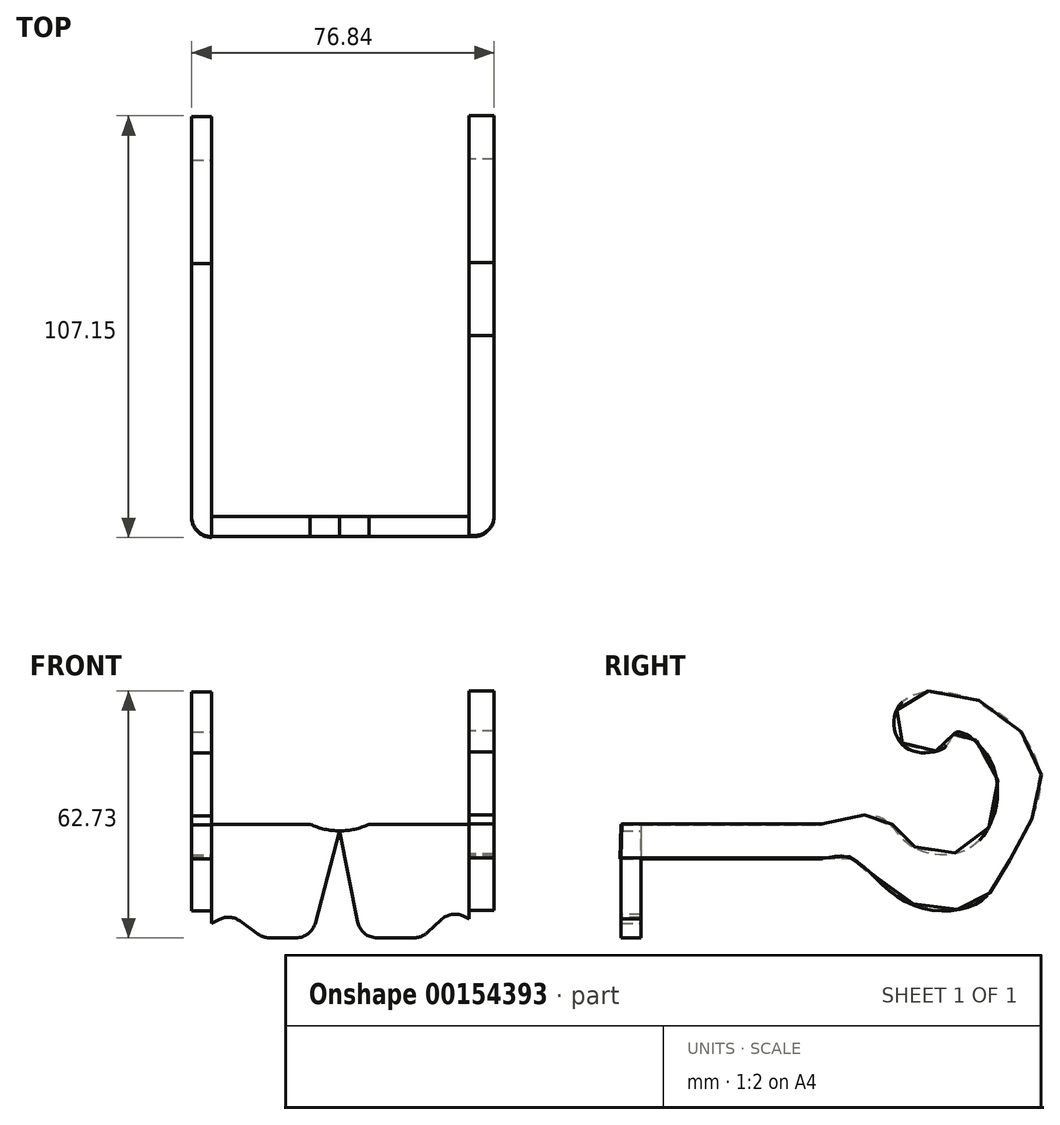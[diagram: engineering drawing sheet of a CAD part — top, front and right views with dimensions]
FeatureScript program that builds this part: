
annotation { "Feature Type Name" : "Feature", "Feature Type Description" : "" }
export const myFeature = defineFeature(function(context is Context, id is Id, definition is map)
    precondition{}
    {
        {
            var Q0;
            Q0=qCreatedBy(makeId("Right.planeOp"),FACE);
            var sketch = newSketch(context, id + "F0", { "sketchPlane" : qUnion([Q0])});
            skLineSegment(sketch, "E0", {"start": v(-32.1, 8.66) * mm, "end": v(18.7, 8.66) * mm});
            skLineSegment(sketch, "E1", {"start": v(-32.33, 0) * mm, "end": v(18.7, 0) * mm});
            skFitSpline(sketch, "E2", {"points": [v(18.7, 0) * mm, v(26.79, 0) * mm, v(39.95, -10.74) * mm, v(58.19, -11.43) * mm, v(66.73, 0) * mm, v(74.58, 20.44) * mm, v(59.57, 39.6) * mm, v(39.02, 39.6) * mm, v(39.72, 28.75) * mm, v(50.34, 28.52) * mm, v(53.1, 32.21) * mm, v(62.58, 23.2) * mm, v(57.03, 3.12) * mm, v(41.1, 3.58) * mm, v(34.4, 10.28) * mm, v(18.7, 8.66) * mm], "startDerivative": vector(163.45, 38.4) * mm, "endDerivative": vector(-264.4, -70.5) * mm});
            skLineSegment(sketch, "E3", {"start": v(-32.1, 8.66) * mm, "end": v(-32.33, 0) * mm});
            skSolve(sketch);
        }
        {
            var Q0;
            Q0=makeQuery(id+"F0.imprint","IMPRINT",FACE,{"disambiguationData":[TD([[makeQuery(id+"F0.imprint","IMPRINT",EDGE,{"derivedFrom":sQuery(id+"F0.wireOp",EDGE,"E0")}),-1.0]])]});
            extrude(context, id + "F1", {"entities" : qUnion([Q0]), "depth" : 5.08 * mm});
        }
        {
            var Q0;
            Q0=makeQuery(id+"F1.opExtrude","SWEPT_EDGE",EDGE,{"disambiguationData":[OSD([sQuery(id+"F0.wireOp",EDGE,"E0"),sQuery(id+"F0.wireOp",EDGE,"E2")])]});
            var Q1;
            Q1=makeQuery(id+"F1.opExtrude","SWEPT_EDGE",EDGE,{"disambiguationData":[OSD([sQuery(id+"F0.wireOp",EDGE,"E1"),sQuery(id+"F0.wireOp",EDGE,"E2")])]});
            fillet(context, id + "F2", {"entities" : qUnion([Q0, Q1]), "radius" : 5.08 * mm, "tangentPropagation" : true, "allowEdgeOverflow" : false});
        }
        {
            var Q0;
            Q0=makeQuery(id+"F1.opExtrude","SWEPT_BODY",BODY,{"disambiguationData":[OSD([sQuery(id+"F0.wireOp",EDGE,"E0"),sQuery(id+"F0.wireOp",EDGE,"E1"),sQuery(id+"F0.wireOp",EDGE,"E2"),sQuery(id+"F0.wireOp",EDGE,"E3")])]});
            var Q1;
            Q1=qCreatedBy(makeId("Origin.pointOp"),VERTEX);
            transform(context, id + "F3", {"entities" : qUnion([Q0]), "transformType" : TransformType.TRANSLATION_3D, "dx" : -67.94 * mm, "dy" : 0 * mm, "dz" : 0 * mm, "makeCopy" : false});
        }
        {
            var Q0;
            Q0=qCreatedBy(makeId("Front.planeOp"),FACE);
            var sketch = newSketch(context, id + "F4", { "sketchPlane" : qUnion([Q0])});
            skLineSegment(sketch, "E4", {"start": v(-40.09, 0) * mm, "end": v(-14.96, 0) * mm});
            skLineSegment(sketch, "E5", {"start": v(25.4, 0) * mm, "end": v(0, 0) * mm});
            skArc(sketch, "E6", {"start": v(-14.96, 0) * mm, "mid": v(-7.48, -1.67) * mm, "end": v(0, 0) * mm});
            skLineSegment(sketch, "E7", {"start": v(-14.64, -28.85) * mm, "end": v(-26.94, -28.85) * mm});
            skLineSegment(sketch, "E8", {"start": v(2705.78, 106.26) * mm, "end": v(2705.78, 111.84) * mm});
            skLineSegment(sketch, "E9", {"start": v(-40.09, 0) * mm, "end": v(-40.09, -25.17) * mm});
            skLineSegment(sketch, "E10", {"start": v(-40.09, -25.17) * mm, "end": v(-35.24, -22.81) * mm});
            skLineSegment(sketch, "E11", {"start": v(-35.24, -22.81) * mm, "end": v(-26.94, -28.85) * mm});
            skLineSegment(sketch, "E12", {"start": v(25.4, 0) * mm, "end": v(25.4, -24) * mm});
            skPoint(sketch, "E12.endSnap0", {"position": v(-37.66, -24) * mm});
            skLineSegment(sketch, "E13", {"start": v(25.4, -24) * mm, "end": v(20.77, -21.9) * mm});
            skLineSegment(sketch, "E14", {"start": v(20.77, -21.9) * mm, "end": v(13.41, -28.85) * mm});
            skLineSegment(sketch, "E15", {"start": v(-2.16, -28.85) * mm, "end": v(13.41, -28.85) * mm});
            skLineSegment(sketch, "E16", {"start": v(-14.64, -28.85) * mm, "end": v(-7.48, -1.67) * mm});
            skLineSegment(sketch, "E17", {"start": v(-7.48, -1.67) * mm, "end": v(-2.16, -28.85) * mm});
            skSolve(sketch);
        }
        {
            var Q0;
            Q0=makeQuery(id+"F4.imprint","IMPRINT",FACE,{"disambiguationData":[TD([[makeQuery(id+"F4.imprint","IMPRINT",EDGE,{"derivedFrom":sQuery(id+"F4.wireOp",EDGE,"E4")}),-1.0]])]});
            extrude(context, id + "F5", {"entities" : qUnion([Q0]), "depth" : 5.08 * mm});
        }
        {
            var Q0;
            Q0=makeQuery(id+"F5.opExtrude","SWEPT_EDGE",EDGE,{"disambiguationData":[OSD([sQuery(id+"F4.wireOp",EDGE,"E7"),sQuery(id+"F4.wireOp",EDGE,"E11")])]});
            var Q1;
            Q1=makeQuery(id+"F5.opExtrude","SWEPT_EDGE",EDGE,{"disambiguationData":[OSD([sQuery(id+"F4.wireOp",EDGE,"E10"),sQuery(id+"F4.wireOp",EDGE,"E11")])]});
            var Q2;
            Q2=makeQuery(id+"F5.opExtrude","SWEPT_EDGE",EDGE,{"disambiguationData":[OSD([sQuery(id+"F4.wireOp",EDGE,"E7"),sQuery(id+"F4.wireOp",EDGE,"E16")])]});
            fillet(context, id + "F6", {"entities" : qUnion([Q0, Q1, Q2]), "radius" : 5.08 * mm, "tangentPropagation" : true, "allowEdgeOverflow" : false});
        }
        {
            var Q0;
            {var subQ1=sQuery(id+"F4.wireOp",EDGE,"E5");Q0=makeQuery(id+"F4.imprint","IMPRINT",FACE,{"disambiguationData":[TD([[makeQuery(id+"F4.imprint","IMPRINT",EDGE,{"derivedFrom":subQ1}),1.0]])]});}
            extrude(context, id + "F7", {"entities" : qUnion([Q0]), "depth" : 5.08 * mm});
        }
        {
            var Q0;
            Q0=makeQuery(id+"F7.opExtrude","SWEPT_EDGE",EDGE,{"disambiguationData":[OSD([sQuery(id+"F4.wireOp",EDGE,"E13"),sQuery(id+"F4.wireOp",EDGE,"E14")])]});
            var Q1;
            Q1=makeQuery(id+"F7.opExtrude","SWEPT_EDGE",EDGE,{"disambiguationData":[OSD([sQuery(id+"F4.wireOp",EDGE,"E14"),sQuery(id+"F4.wireOp",EDGE,"E15")])]});
            var Q2;
            Q2=makeQuery(id+"F7.opExtrude","SWEPT_EDGE",EDGE,{"disambiguationData":[OSD([sQuery(id+"F4.wireOp",EDGE,"E15"),sQuery(id+"F4.wireOp",EDGE,"E17")])]});
            fillet(context, id + "F8", {"entities" : qUnion([Q0, Q1, Q2]), "radius" : 5.08 * mm, "tangentPropagation" : true, "allowEdgeOverflow" : false});
        }
        {
            var Q0;
            Q0=qCreatedBy(makeId("Right.planeOp"),FACE);
            var sketch = newSketch(context, id + "F9", { "sketchPlane" : qUnion([Q0])});
            skLineSegment(sketch, "E18", {"start": v(71.95, 5.52) * mm, "end": v(122.75, 5.52) * mm});
            skLineSegment(sketch, "E19", {"start": v(71.72, -3.14) * mm, "end": v(122.75, -3.14) * mm});
            skFitSpline(sketch, "E20", {"points": [v(122.75, -3.14) * mm, v(130.83, -3.14) * mm, v(144, -13.88) * mm, v(162.23, -14.57) * mm, v(170.78, -3.14) * mm, v(178.63, 17.3) * mm, v(163.62, 36.46) * mm, v(143.07, 36.46) * mm, v(143.76, 25.6) * mm, v(154.38, 25.37) * mm, v(157.15, 29.07) * mm, v(166.62, 20.06) * mm, v(161.08, -0.03) * mm, v(145.14, 0.44) * mm, v(138.45, 7.13) * mm, v(122.75, 5.52) * mm], "startDerivative": vector(163.45, 38.4) * mm, "endDerivative": vector(-264.4, -70.5) * mm});
            skLineSegment(sketch, "E21", {"start": v(71.95, 5.52) * mm, "end": v(71.72, -3.14) * mm});
            skSolve(sketch);
        }
        {
            var Q0;
            Q0=makeQuery(id+"F9.imprint","IMPRINT",FACE,{"disambiguationData":[TD([[makeQuery(id+"F9.imprint","IMPRINT",EDGE,{"derivedFrom":sQuery(id+"F9.wireOp",EDGE,"E18")}),-1.0]])]});
            extrude(context, id + "F10", {"entities" : qUnion([Q0]), "depth" : 6.35 * mm});
        }
        {
            var Q0;
            Q0=makeQuery(id+"F10.opExtrude","SWEPT_BODY",BODY,{"disambiguationData":[OSD([sQuery(id+"F9.wireOp",EDGE,"E18"),sQuery(id+"F9.wireOp",EDGE,"E19"),sQuery(id+"F9.wireOp",EDGE,"E20"),sQuery(id+"F9.wireOp",EDGE,"E21")])]});
            var Q1;
            Q1=qCreatedBy(makeId("Origin.pointOp"),VERTEX);
            transform(context, id + "F11", {"entities" : qUnion([Q0]), "transformType" : TransformType.TRANSLATION_3D, "dx" : 25.4 * mm, "dy" : -76.83 * mm, "dz" : -5.46 * mm, "makeCopy" : false});
        }
        {
            var Q0;
            Q0=makeQuery(id+"F1.opExtrude","SWEPT_BODY",BODY,{"disambiguationData":[OSD([sQuery(id+"F0.wireOp",EDGE,"E0"),sQuery(id+"F0.wireOp",EDGE,"E1"),sQuery(id+"F0.wireOp",EDGE,"E2"),sQuery(id+"F0.wireOp",EDGE,"E3")])]});
            var Q1;
            Q1=qCreatedBy(makeId("Origin.pointOp"),VERTEX);
            transform(context, id + "F12", {"entities" : qUnion([Q0]), "transformType" : TransformType.TRANSLATION_3D, "dx" : 22.86 * mm, "dy" : 26.99 * mm, "dz" : -8.83 * mm, "makeCopy" : false});
        }
        {
            var Q0;
            Q0=makeQuery(id+"F1.opExtrude","CAP_EDGE",EDGE,{"disambiguationData":[OSD([sQuery(id+"F0.wireOp",EDGE,"E3")])],"isStart":true});
            var Q1;
            Q1=makeQuery(id+"F10.opExtrude","CAP_EDGE",EDGE,{"disambiguationData":[OSD([sQuery(id+"F9.wireOp",EDGE,"E21")])],"isStart":false});
            fillet(context, id + "F13", {"entities" : qUnion([Q0, Q1]), "radius" : 5.08 * mm, "tangentPropagation" : true, "allowEdgeOverflow" : false});
        }
    });
